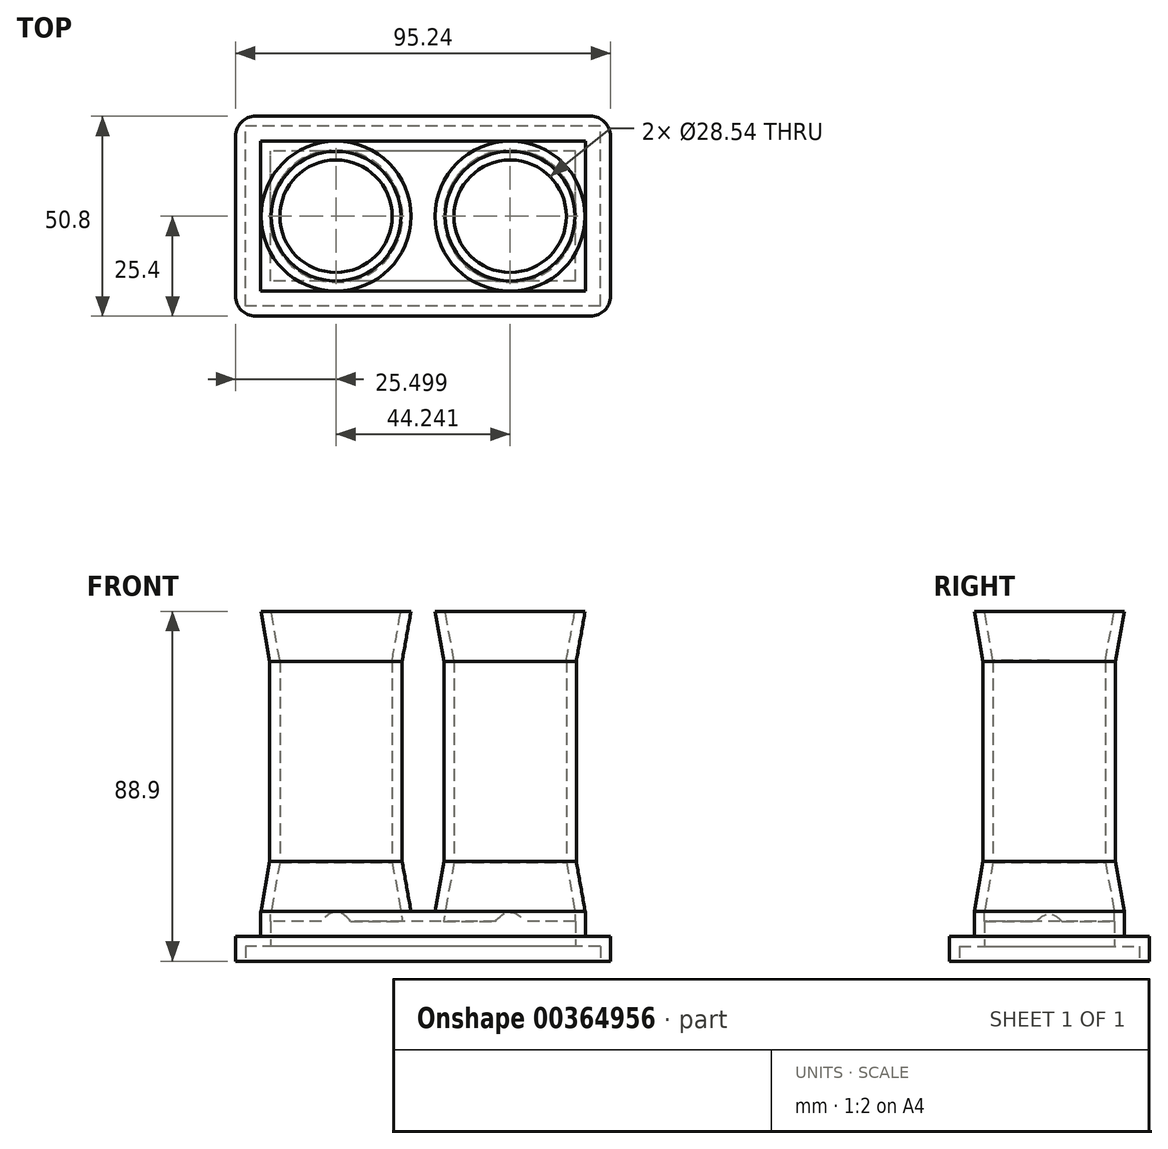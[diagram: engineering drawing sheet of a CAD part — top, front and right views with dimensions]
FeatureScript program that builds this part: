
annotation { "Feature Type Name" : "Feature", "Feature Type Description" : "" }
export const myFeature = defineFeature(function(context is Context, id is Id, definition is map)
    precondition{}
    {
        {
            var Q0;
            Q0=qCreatedBy(makeId("Top.planeOp"),FACE);
            var sketch = newSketch(context, id + "F0", { "sketchPlane" : qUnion([Q0])});
            skLineSegment(sketch, "E0.bottom", {"start": v(47.63, -25.4) * mm, "end": v(-47.63, -25.4) * mm});
            skLineSegment(sketch, "E0.top", {"start": v(47.63, 25.4) * mm, "end": v(-47.63, 25.4) * mm});
            skLineSegment(sketch, "E0.left", {"start": v(47.63, -25.4) * mm, "end": v(47.63, 25.4) * mm});
            skLineSegment(sketch, "E0.right", {"start": v(-47.63, -25.4) * mm, "end": v(-47.63, 25.4) * mm});
            skPoint(sketch, "E0.middle", {"position": v(0, 0) * mm});
            skSolve(sketch);
        }
        {
            var Q0;
            Q0=qSketchRegion(id+"F0",true);
            extrude(context, id + "F1", {"entities" : qUnion([Q0]), "depth" : 6.35 * mm});
        }
        {
            var Q0;
            Q0=makeQuery(id+"F1.opExtrude","CAP_FACE",FACE,{"disambiguationData":[OSD([sQuery(id+"F0.wireOp",EDGE,"E0.bottom"),sQuery(id+"F0.wireOp",EDGE,"E0.top"),sQuery(id+"F0.wireOp",EDGE,"E0.left"),sQuery(id+"F0.wireOp",EDGE,"E0.right")])],"isStart":false});
            var sketch = newSketch(context, id + "F2", { "sketchPlane" : qUnion([Q0])});
            skLineSegment(sketch, "E1.bottom", {"start": v(41.28, -19.05) * mm, "end": v(-41.28, -19.05) * mm});
            skLineSegment(sketch, "E1.top", {"start": v(41.28, 19.05) * mm, "end": v(-41.28, 19.05) * mm});
            skLineSegment(sketch, "E1.left", {"start": v(41.28, -19.05) * mm, "end": v(41.28, 19.05) * mm});
            skLineSegment(sketch, "E1.right", {"start": v(-41.28, -19.05) * mm, "end": v(-41.28, 19.05) * mm});
            skPoint(sketch, "E1.middle", {"position": v(0, 0) * mm});
            skSolve(sketch);
        }
        {
            var Q0;
            Q0=makeQuery(id+"F2.imprint","IMPRINT",FACE,{"disambiguationData":[TD([[makeQuery(id+"F2.imprint","IMPRINT",EDGE,{"derivedFrom":sQuery(id+"F2.wireOp",EDGE,"E1.bottom")}),-1.0]])]});
            extrude(context, id + "F3", {"entities" : qUnion([Q0]), "operationType" : NewBodyOperationType.ADD, "depth" : 6.35 * mm});
        }
        {
            var Q0;
            Q0=makeQuery(id+"F3.opExtrude","CAP_FACE",FACE,{"disambiguationData":[OSD([sQuery(id+"F2.wireOp",EDGE,"E1.bottom"),sQuery(id+"F2.wireOp",EDGE,"E1.top"),sQuery(id+"F2.wireOp",EDGE,"E1.left"),sQuery(id+"F2.wireOp",EDGE,"E1.right")])],"isStart":false});
            var sketch = newSketch(context, id + "F4", { "sketchPlane" : qUnion([Q0])});
            skCircle(sketch, "E2", {"center": v(-22.12, 0) * mm, "radius": 19.05 * mm});
            skPoint(sketch, "E2.centerSnap0", {"position": v(-41.28, 0) * mm});
            skCircle(sketch, "E3.MirrorC", {"center": v(22.12, 0) * mm, "radius": 19.05 * mm});
            skLineSegment(sketch, "E4", {"start": v(-22.12, 0) * mm, "end": v(22.12, 0) * mm, "construction": true});
            skSolve(sketch);
        }
        {
            var Q0;
            Q0=qSketchRegion(id+"F4",true);
            extrude(context, id + "F5", {"entities" : qUnion([Q0]), "operationType" : NewBodyOperationType.ADD, "depth" : 12.7 * mm, "hasDraft" : true, "draftAngle" : 10 * degree, "draftPullDirection" : true});
        }
        {
            var Q0;
            Q0=makeQuery(id+"F5.opExtrude","CAP_FACE",FACE,{"disambiguationData":[OSD([sQuery(id+"F4.wireOp",EDGE,"E2")])],"isStart":false});
            var Q1;
            Q1=makeQuery(id+"F5.opExtrude","CAP_FACE",FACE,{"disambiguationData":[OSD([sQuery(id+"F4.wireOp",EDGE,"E3.MirrorC")])],"isStart":false});
            extrude(context, id + "F6", {"entities" : qUnion([Q0, Q1]), "operationType" : NewBodyOperationType.ADD, "depth" : 50.8 * mm});
        }
        {
            var Q0;
            Q0=makeQuery(id+"F6.opExtrude","CAP_FACE",FACE,{"disambiguationData":[OSD([sQuery(id+"F4.wireOp",EDGE,"E3.MirrorC")])],"isStart":false});
            var Q1;
            Q1=makeQuery(id+"F6.opExtrude","CAP_FACE",FACE,{"disambiguationData":[OSD([sQuery(id+"F4.wireOp",EDGE,"E2")])],"isStart":false});
            extrude(context, id + "F7", {"entities" : qUnion([Q0, Q1]), "operationType" : NewBodyOperationType.ADD, "depth" : 12.7 * mm, "hasDraft" : true, "draftAngle" : 10 * degree});
        }
        {
            var Q0;
            Q0=makeQuery(id+"F7.opExtrude","CAP_FACE",FACE,{"disambiguationData":[OSD([sQuery(id+"F4.wireOp",EDGE,"E2")])],"isStart":false});
            var Q1;
            Q1=makeQuery(id+"F7.opExtrude","CAP_FACE",FACE,{"disambiguationData":[OSD([sQuery(id+"F4.wireOp",EDGE,"E3.MirrorC")])],"isStart":false});
            var Q2;
            Q2=makeQuery(id+"F1.opExtrude","CAP_FACE",FACE,{"disambiguationData":[OSD([sQuery(id+"F0.wireOp",EDGE,"E0.bottom"),sQuery(id+"F0.wireOp",EDGE,"E0.top"),sQuery(id+"F0.wireOp",EDGE,"E0.left"),sQuery(id+"F0.wireOp",EDGE,"E0.right")])],"isStart":true});
            shell(context, id + "F8", {"entities" : qUnion([Q0, Q1, Q2]), "thickness" : 2.54 * mm});
        }
        {
            var Q0;
            Q0=makeQuery(id+"F1.opExtrude","SWEPT_EDGE",EDGE,{"disambiguationData":[OSD([sQuery(id+"F0.wireOp",EDGE,"E0.bottom"),sQuery(id+"F0.wireOp",EDGE,"E0.right")])]});
            var Q1;
            Q1=makeQuery(id+"F1.opExtrude","SWEPT_EDGE",EDGE,{"disambiguationData":[OSD([sQuery(id+"F0.wireOp",EDGE,"E0.bottom"),sQuery(id+"F0.wireOp",EDGE,"E0.left")])]});
            var Q2;
            Q2=makeQuery(id+"F1.opExtrude","SWEPT_EDGE",EDGE,{"disambiguationData":[OSD([sQuery(id+"F0.wireOp",EDGE,"E0.top"),sQuery(id+"F0.wireOp",EDGE,"E0.left")])]});
            var Q3;
            Q3=makeQuery(id+"F1.opExtrude","SWEPT_EDGE",EDGE,{"disambiguationData":[OSD([sQuery(id+"F0.wireOp",EDGE,"E0.top"),sQuery(id+"F0.wireOp",EDGE,"E0.right")])]});
            fillet(context, id + "F9", {"entities" : qUnion([Q0, Q1, Q2, Q3]), "radius" : 5.08 * mm, "tangentPropagation" : true, "allowEdgeOverflow" : false});
        }
    });
